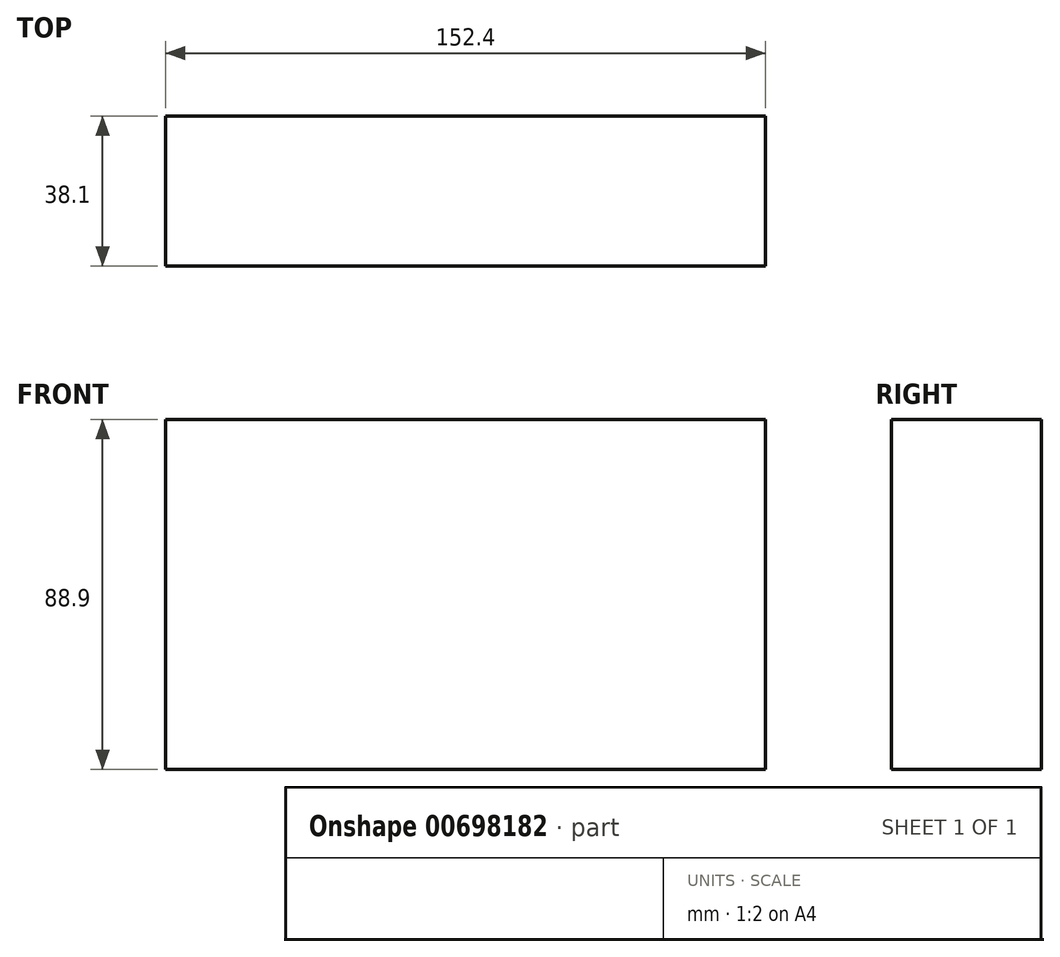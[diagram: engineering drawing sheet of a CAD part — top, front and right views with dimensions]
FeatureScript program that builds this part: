
annotation { "Feature Type Name" : "Feature", "Feature Type Description" : "" }
export const myFeature = defineFeature(function(context is Context, id is Id, definition is map)
    precondition{}
    {
        {
            var Q0;
            Q0=qCreatedBy(makeId("Front.planeOp"),FACE);
            var sketch = newSketch(context, id + "F0", { "sketchPlane" : qUnion([Q0])});
            skLineSegment(sketch, "E0.bottom", {"start": v(0, 0) * mm, "end": v(-152.4, 0) * mm});
            skLineSegment(sketch, "E0.top", {"start": v(0, 88.9) * mm, "end": v(-152.4, 88.9) * mm});
            skLineSegment(sketch, "E0.left", {"start": v(0, 0) * mm, "end": v(0, 88.9) * mm});
            skLineSegment(sketch, "E0.right", {"start": v(-152.4, 0) * mm, "end": v(-152.4, 88.9) * mm});
            skSolve(sketch);
        }
        {
            var Q0;
            Q0=makeQuery(id+"F0.imprint","IMPRINT",FACE,{"disambiguationData":[TD([[makeQuery(id+"F0.imprint","IMPRINT",EDGE,{"derivedFrom":sQuery(id+"F0.wireOp",EDGE,"E0.bottom")}),-1.0]])]});
            extrude(context, id + "F1", {"entities" : qUnion([Q0]), "depth" : 38.1 * mm, "offsetDistance" : 25.4 * mm});
        }
    });
